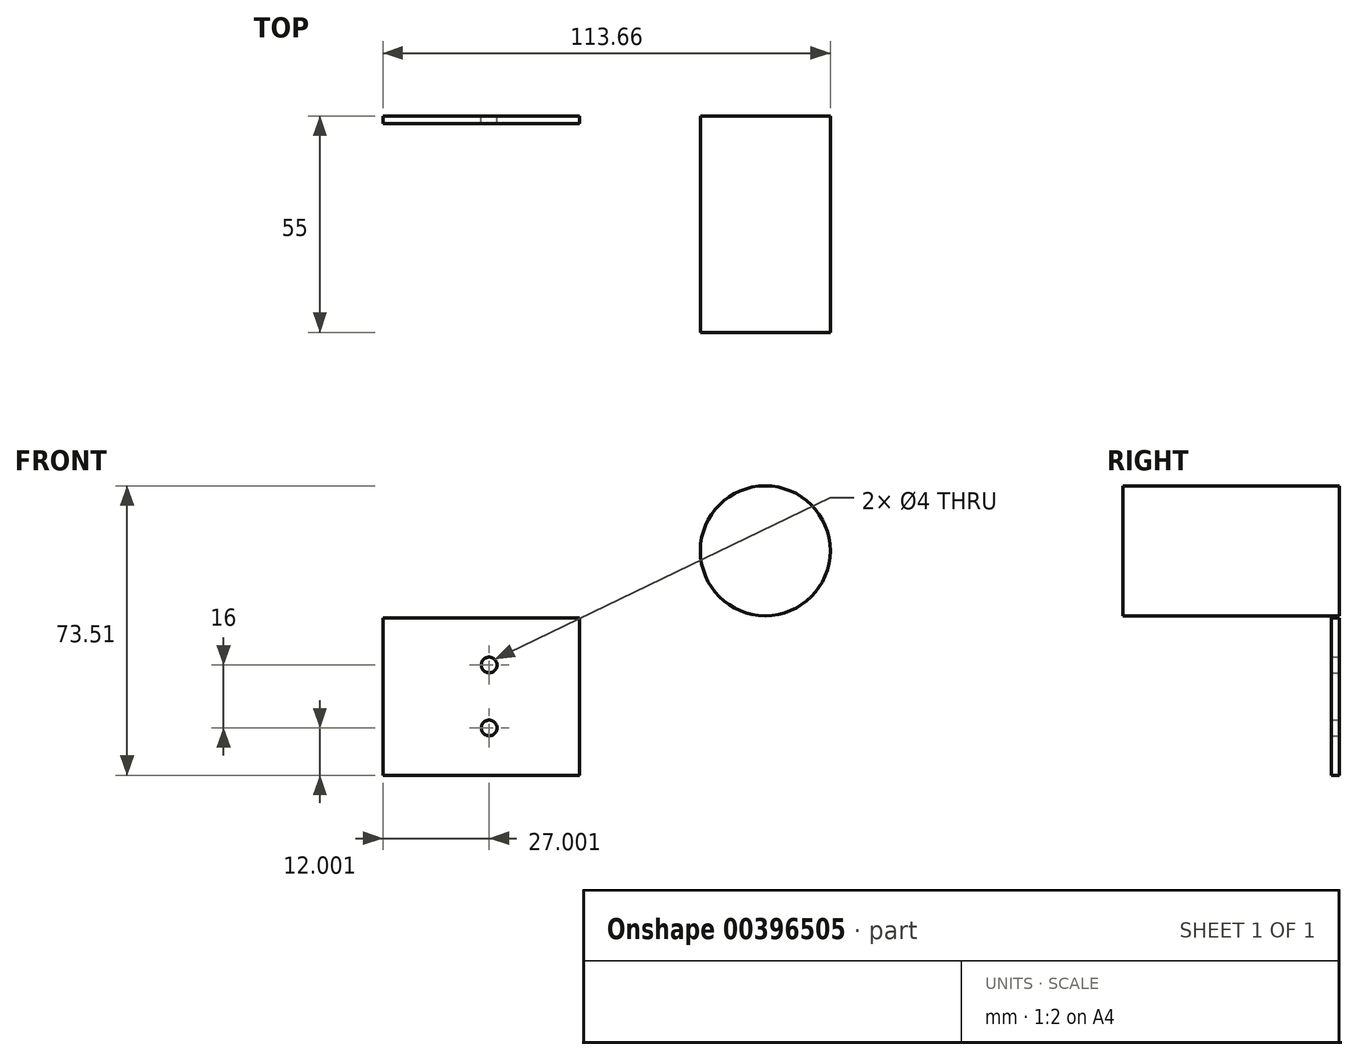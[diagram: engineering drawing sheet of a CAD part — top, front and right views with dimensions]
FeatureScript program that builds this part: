
annotation { "Feature Type Name" : "Feature", "Feature Type Description" : "" }
export const myFeature = defineFeature(function(context is Context, id is Id, definition is map)
    precondition{}
    {
        {
            var Q0;
            Q0=qCreatedBy(makeId("Front.planeOp"),FACE);
            var sketch = newSketch(context, id + "F0", { "sketchPlane" : qUnion([Q0])});
            skLineSegment(sketch, "E0.bottom", {"start": v(-54.09, 2.64) * mm, "end": v(-4.09, 2.64) * mm});
            skLineSegment(sketch, "E0.top", {"start": v(-54.09, -37.36) * mm, "end": v(-4.09, -37.36) * mm});
            skLineSegment(sketch, "E0.left", {"start": v(-54.09, 2.64) * mm, "end": v(-54.09, -37.36) * mm});
            skLineSegment(sketch, "E0.right", {"start": v(-4.09, 2.64) * mm, "end": v(-4.09, -37.36) * mm});
            skCircle(sketch, "E1", {"center": v(-27.09, -25.36) * mm, "radius": 2 * mm});
            skCircle(sketch, "E2", {"center": v(-27.09, -9.36) * mm, "radius": 2 * mm});
            skSolve(sketch);
        }
        {
            var Q0;
            Q0 = qSketchRegion(id + "F0", true);
            extrude(context, id + "F1", {"entities" : qUnion([Q0]), "depth" : 2 * mm});
        }
        {
            var Q0;
            Q0=qCreatedBy(makeId("Front.planeOp"),FACE);
            var sketch = newSketch(context, id + "F2", { "sketchPlane" : qUnion([Q0])});
            skCircle(sketch, "E3", {"center": v(43.07, 19.65) * mm, "radius": 16.5 * mm});
            skSolve(sketch);
        }
        {
            var Q0;
            Q0 = qSketchRegion(id + "F2", true);
            extrude(context, id + "F3", {"entities" : qUnion([Q0]), "depth" : 55 * mm});
        }
    });
